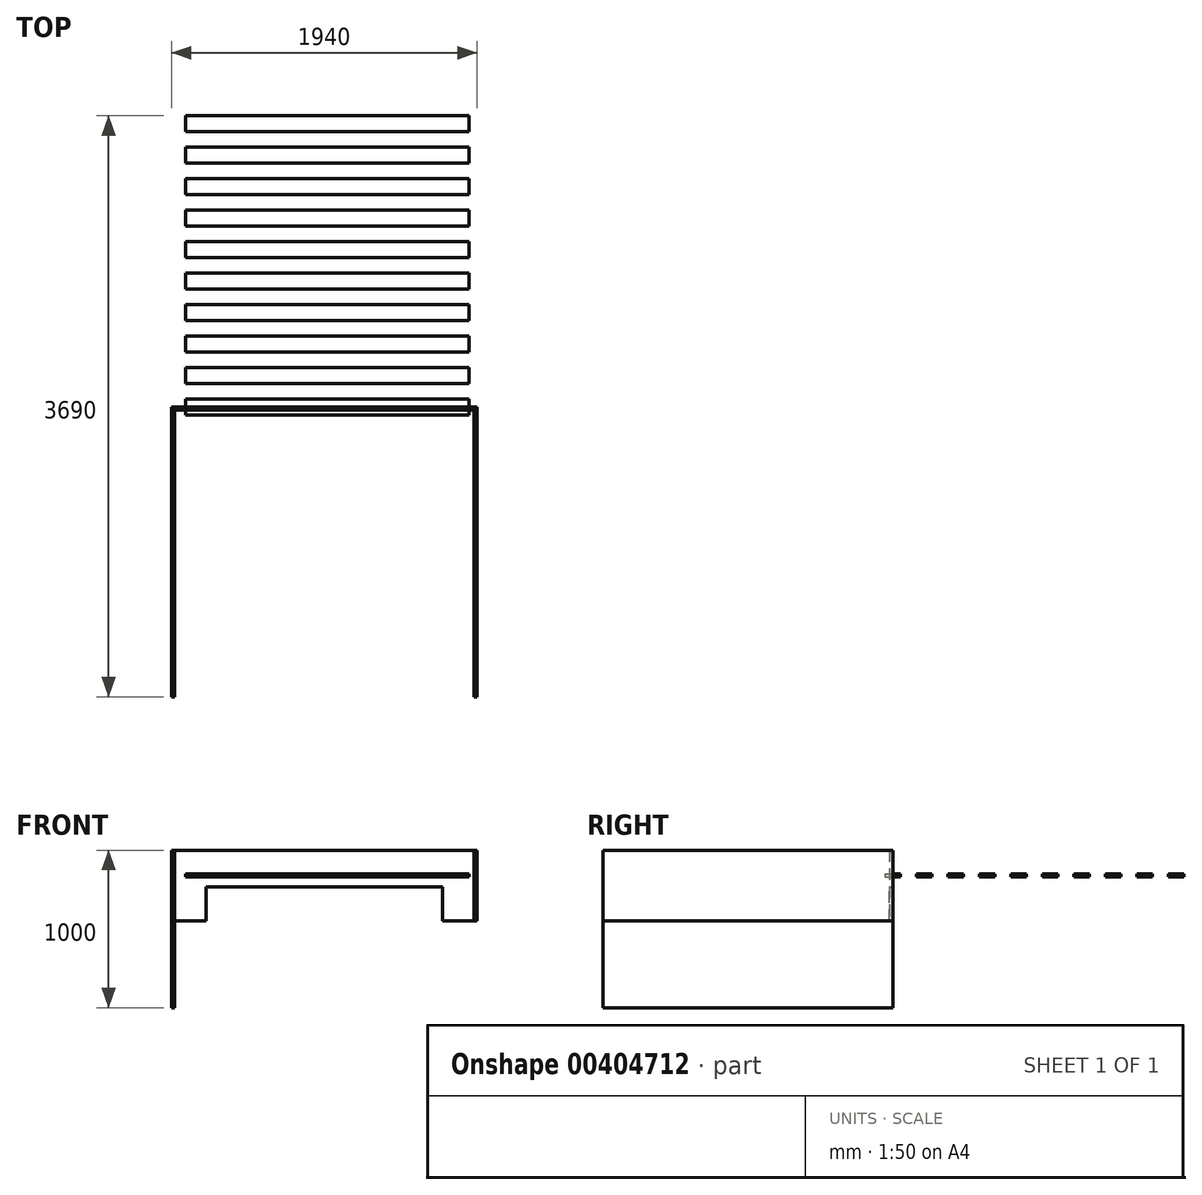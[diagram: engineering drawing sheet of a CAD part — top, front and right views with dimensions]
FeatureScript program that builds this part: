
annotation { "Feature Type Name" : "Feature", "Feature Type Description" : "" }
export const myFeature = defineFeature(function(context is Context, id is Id, definition is map)
    precondition{}
    {
        {
            var Q0;
            Q0=qCreatedBy(makeId("Front.planeOp"),FACE);
            var sketch = newSketch(context, id + "F0", { "sketchPlane" : qUnion([Q0])});
            skLineSegment(sketch, "E0", {"start": v(-968.6, 169.08) * mm, "end": v(931.4, 169.08) * mm});
            skLineSegment(sketch, "E1", {"start": v(-968.6, 169.08) * mm, "end": v(-968.6, -280.92) * mm});
            skLineSegment(sketch, "E2", {"start": v(-968.6, -280.92) * mm, "end": v(-768.6, -280.92) * mm});
            skLineSegment(sketch, "E3", {"start": v(-768.6, -280.92) * mm, "end": v(-768.6, -65.08) * mm});
            skLineSegment(sketch, "E4", {"start": v(-768.6, -65.08) * mm, "end": v(731.4, -65.08) * mm});
            skLineSegment(sketch, "E5", {"start": v(731.4, -65.08) * mm, "end": v(731.4, -280.92) * mm});
            skLineSegment(sketch, "E6", {"start": v(731.4, -280.92) * mm, "end": v(931.4, -280.92) * mm});
            skLineSegment(sketch, "E7", {"start": v(931.4, -280.92) * mm, "end": v(931.4, 169.08) * mm});
            skSolve(sketch);
        }
        {
            var Q0;
            Q0 = qSketchRegion(id + "F0", true);
            extrude(context, id + "F1", {"entities" : qUnion([Q0]), "depth" : 20 * mm});
        }
        {
            var Q0;
            Q0=qCreatedBy(makeId("Top.planeOp"),FACE);
            var sketch = newSketch(context, id + "F2", { "sketchPlane" : qUnion([Q0])});
            skLineSegment(sketch, "E8.bottom", {"start": v(900, -50) * mm, "end": v(-900, -50) * mm});
            skLineSegment(sketch, "E8.top", {"start": v(900, 50) * mm, "end": v(-900, 50) * mm});
            skLineSegment(sketch, "E8.left", {"start": v(900, -50) * mm, "end": v(900, 50) * mm});
            skLineSegment(sketch, "E8.right", {"start": v(-900, -50) * mm, "end": v(-900, 50) * mm});
            skPoint(sketch, "E8.middle", {"position": v(0, 0) * mm});
            skLineSegment(sketch, "E9.MirrorCS", {"start": v(900, 150) * mm, "end": v(-900, 150) * mm});
            skLineSegment(sketch, "E10.MirrorCS", {"start": v(900, 250) * mm, "end": v(-900, 250) * mm});
            skLineSegment(sketch, "E11", {"start": v(-900, 150) * mm, "end": v(-900, 250) * mm});
            skLineSegment(sketch, "E12", {"start": v(900, 150) * mm, "end": v(900, 250) * mm});
            skLineSegment(sketch, "E13.MirrorCS", {"start": v(900, 350) * mm, "end": v(-900, 350) * mm});
            skLineSegment(sketch, "E14.MirrorCS", {"start": v(900, 450) * mm, "end": v(-900, 450) * mm});
            skLineSegment(sketch, "E15", {"start": v(-900, 350) * mm, "end": v(-900, 450) * mm});
            skLineSegment(sketch, "E16", {"start": v(900, 350) * mm, "end": v(900, 450) * mm});
            skLineSegment(sketch, "E17.MirrorCS", {"start": v(900, 550) * mm, "end": v(-900, 550) * mm});
            skLineSegment(sketch, "E18.MirrorCS", {"start": v(900, 650) * mm, "end": v(-900, 650) * mm});
            skLineSegment(sketch, "E19", {"start": v(-900, 550) * mm, "end": v(-900, 650) * mm});
            skLineSegment(sketch, "E20", {"start": v(900, 550) * mm, "end": v(900, 650) * mm});
            skLineSegment(sketch, "E21.MirrorCS", {"start": v(900, 750) * mm, "end": v(-900, 750) * mm});
            skLineSegment(sketch, "E22.MirrorCS", {"start": v(900, 850) * mm, "end": v(-900, 850) * mm});
            skLineSegment(sketch, "E23", {"start": v(-900, 750) * mm, "end": v(-900, 850) * mm});
            skLineSegment(sketch, "E24", {"start": v(900, 750) * mm, "end": v(900, 850) * mm});
            skLineSegment(sketch, "E25.MirrorCS", {"start": v(900, 950) * mm, "end": v(-900, 950) * mm});
            skLineSegment(sketch, "E26.MirrorCS", {"start": v(900, 1050) * mm, "end": v(-900, 1050) * mm});
            skLineSegment(sketch, "E27", {"start": v(-900, 950) * mm, "end": v(-900, 1050) * mm});
            skLineSegment(sketch, "E28", {"start": v(900, 950) * mm, "end": v(900, 1050) * mm});
            skLineSegment(sketch, "E29.MirrorCS", {"start": v(900, 1150) * mm, "end": v(-900, 1150) * mm});
            skLineSegment(sketch, "E30.MirrorCS", {"start": v(900, 1250) * mm, "end": v(-900, 1250) * mm});
            skLineSegment(sketch, "E31", {"start": v(-900, 1150) * mm, "end": v(-900, 1250) * mm});
            skLineSegment(sketch, "E32", {"start": v(900, 1150) * mm, "end": v(900, 1250) * mm});
            skLineSegment(sketch, "E33.MirrorCS", {"start": v(900, 1550) * mm, "end": v(-900, 1550) * mm});
            skLineSegment(sketch, "E34.MirrorCS", {"start": v(900, 1650) * mm, "end": v(-900, 1650) * mm});
            skLineSegment(sketch, "E35", {"start": v(-900, 1550) * mm, "end": v(-900, 1650) * mm});
            skLineSegment(sketch, "E36", {"start": v(900, 1550) * mm, "end": v(900, 1650) * mm});
            skLineSegment(sketch, "E37.MirrorCS", {"start": v(900, 1350) * mm, "end": v(-900, 1350) * mm});
            skLineSegment(sketch, "E38.MirrorCS", {"start": v(900, 1450) * mm, "end": v(-900, 1450) * mm});
            skLineSegment(sketch, "E39", {"start": v(-900, 1350) * mm, "end": v(-900, 1450) * mm});
            skLineSegment(sketch, "E40", {"start": v(900, 1350) * mm, "end": v(900, 1450) * mm});
            skLineSegment(sketch, "E41.MirrorCS", {"start": v(900, 1750) * mm, "end": v(-900, 1750) * mm});
            skLineSegment(sketch, "E42.MirrorCS", {"start": v(900, 1850) * mm, "end": v(-900, 1850) * mm});
            skLineSegment(sketch, "E43", {"start": v(-900, 1750) * mm, "end": v(-900, 1850) * mm});
            skLineSegment(sketch, "E44", {"start": v(900, 1750) * mm, "end": v(900, 1850) * mm});
            skSolve(sketch);
        }
        {
            var Q0;
            Q0=makeQuery(id+"F2.imprint","IMPRINT",FACE,{"disambiguationData":[TD([[makeQuery(id+"F2.imprint","IMPRINT",EDGE,{"derivedFrom":sQuery(id+"F2.wireOp",EDGE,"E41.MirrorCS")}),-1.0]])]});
            var Q1;
            Q1=makeQuery(id+"F2.imprint","IMPRINT",FACE,{"disambiguationData":[TD([[makeQuery(id+"F2.imprint","IMPRINT",EDGE,{"derivedFrom":sQuery(id+"F2.wireOp",EDGE,"E33.MirrorCS")}),-1.0]])]});
            var Q2;
            Q2=makeQuery(id+"F2.imprint","IMPRINT",FACE,{"disambiguationData":[TD([[makeQuery(id+"F2.imprint","IMPRINT",EDGE,{"derivedFrom":sQuery(id+"F2.wireOp",EDGE,"E37.MirrorCS")}),-1.0]])]});
            var Q3;
            Q3=makeQuery(id+"F2.imprint","IMPRINT",FACE,{"disambiguationData":[TD([[makeQuery(id+"F2.imprint","IMPRINT",EDGE,{"derivedFrom":sQuery(id+"F2.wireOp",EDGE,"E29.MirrorCS")}),-1.0]])]});
            var Q4;
            Q4=makeQuery(id+"F2.imprint","IMPRINT",FACE,{"disambiguationData":[TD([[makeQuery(id+"F2.imprint","IMPRINT",EDGE,{"derivedFrom":sQuery(id+"F2.wireOp",EDGE,"E25.MirrorCS")}),-1.0]])]});
            var Q5;
            Q5=makeQuery(id+"F2.imprint","IMPRINT",FACE,{"disambiguationData":[TD([[makeQuery(id+"F2.imprint","IMPRINT",EDGE,{"derivedFrom":sQuery(id+"F2.wireOp",EDGE,"E21.MirrorCS")}),-1.0]])]});
            var Q6;
            Q6=makeQuery(id+"F2.imprint","IMPRINT",FACE,{"disambiguationData":[TD([[makeQuery(id+"F2.imprint","IMPRINT",EDGE,{"derivedFrom":sQuery(id+"F2.wireOp",EDGE,"E17.MirrorCS")}),-1.0]])]});
            var Q7;
            Q7=makeQuery(id+"F2.imprint","IMPRINT",FACE,{"disambiguationData":[TD([[makeQuery(id+"F2.imprint","IMPRINT",EDGE,{"derivedFrom":sQuery(id+"F2.wireOp",EDGE,"E13.MirrorCS")}),-1.0]])]});
            var Q8;
            Q8=makeQuery(id+"F2.imprint","IMPRINT",FACE,{"disambiguationData":[TD([[makeQuery(id+"F2.imprint","IMPRINT",EDGE,{"derivedFrom":sQuery(id+"F2.wireOp",EDGE,"E9.MirrorCS")}),-1.0]])]});
            var Q9;
            Q9=makeQuery(id+"F2.imprint","IMPRINT",FACE,{"disambiguationData":[TD([[makeQuery(id+"F2.imprint","IMPRINT",EDGE,{"derivedFrom":sQuery(id+"F2.wireOp",EDGE,"E8.bottom")}),-1.0]])]});
            extrude(context, id + "F3", {"entities" : qUnion([Q0, Q1, Q2, Q3, Q4, Q5, Q6, Q7, Q8, Q9]), "depth" : 20 * mm});
        }
        {
            var Q0;
            Q0=qCreatedBy(makeId("Front.planeOp"),FACE);
            var sketch = newSketch(context, id + "F4", { "sketchPlane" : qUnion([Q0])});
            skLineSegment(sketch, "E45.bottom", {"start": v(-968.6, 169.08) * mm, "end": v(-988.6, 169.08) * mm});
            skLineSegment(sketch, "E45.top", {"start": v(-968.6, -830.92) * mm, "end": v(-988.6, -830.92) * mm});
            skLineSegment(sketch, "E45.left", {"start": v(-968.6, 169.08) * mm, "end": v(-968.6, -830.92) * mm});
            skLineSegment(sketch, "E45.right", {"start": v(-988.6, 169.08) * mm, "end": v(-988.6, -830.92) * mm});
            skLineSegment(sketch, "E46.bottom", {"start": v(931.4, 169.08) * mm, "end": v(951.4, 169.08) * mm});
            skLineSegment(sketch, "E46.top", {"start": v(931.4, -280.92) * mm, "end": v(951.4, -280.92) * mm});
            skLineSegment(sketch, "E46.left", {"start": v(931.4, 169.08) * mm, "end": v(931.4, -280.92) * mm});
            skLineSegment(sketch, "E46.right", {"start": v(951.4, 169.08) * mm, "end": v(951.4, -280.92) * mm});
            skSolve(sketch);
        }
        {
            var Q0;
            Q0 = qSketchRegion(id + "F4", true);
            extrude(context, id + "F5", {"entities" : qUnion([Q0]), "depth" : 1840 * mm});
        }
    });
